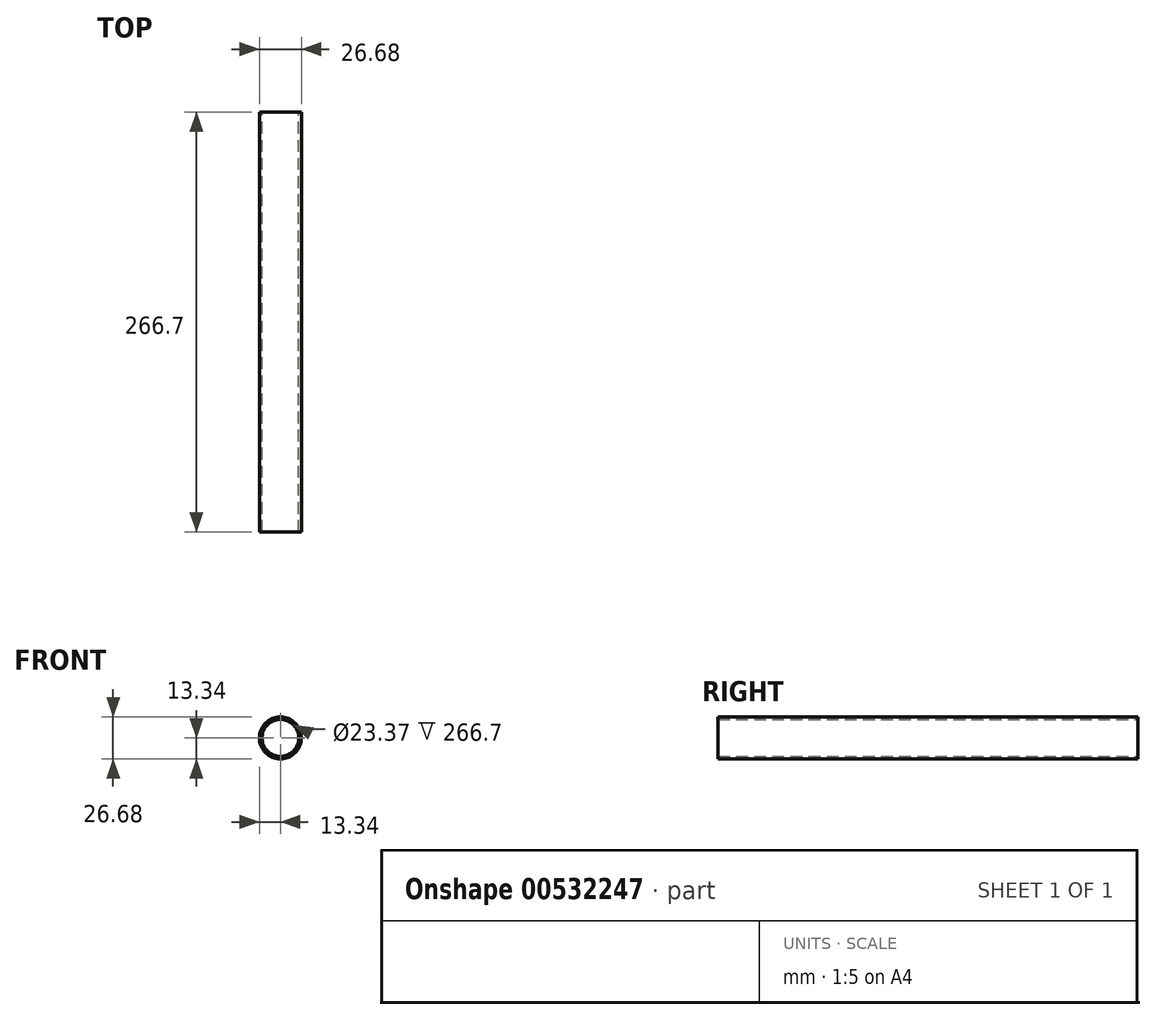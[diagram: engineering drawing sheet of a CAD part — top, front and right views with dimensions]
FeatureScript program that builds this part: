
annotation { "Feature Type Name" : "Feature", "Feature Type Description" : "" }
export const myFeature = defineFeature(function(context is Context, id is Id, definition is map)
    precondition{}
    {
        {
            var Q0;
            Q0=qCreatedBy(makeId("Front.planeOp"),FACE);
            var sketch = newSketch(context, id + "F0", { "sketchPlane" : qUnion([Q0])});
            skCircle(sketch, "E0", {"center": v(0, 0) * mm, "radius": 11.68 * mm});
            skCircle(sketch, "E1", {"center": v(0, 0) * mm, "radius": 13.34 * mm});
            skSolve(sketch);
        }
        {
            var Q0;
            Q0=makeQuery(id+"F0.imprint","IMPRINT",FACE,{"disambiguationData":[TD([[makeQuery(id+"F0.imprint","IMPRINT",EDGE,{"derivedFrom":sQuery(id+"F0.wireOp",EDGE,"E0")}),-1.0]])]});
            extrude(context, id + "F1", {"entities" : qUnion([Q0]), "depth" : 266.7 * mm, "offsetDistance" : 25.4 * mm});
        }
    });
